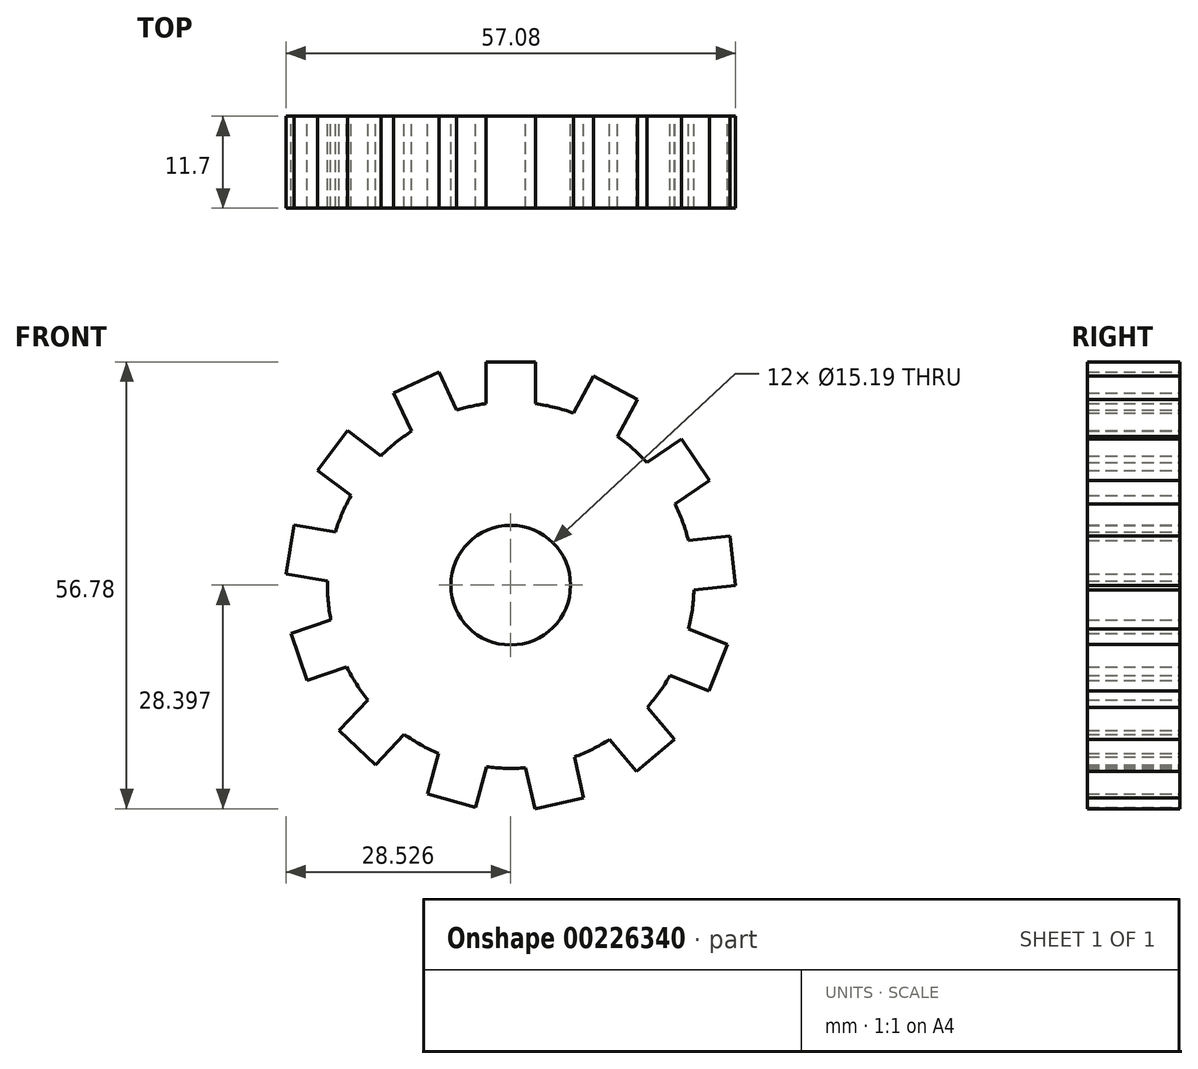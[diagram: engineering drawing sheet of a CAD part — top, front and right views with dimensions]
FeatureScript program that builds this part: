
annotation { "Feature Type Name" : "Feature", "Feature Type Description" : "" }
export const myFeature = defineFeature(function(context is Context, id is Id, definition is map)
    precondition{}
    {
        {
            var Q0;
            Q0=qCreatedBy(makeId("Front.planeOp"),FACE);
            var sketch = newSketch(context, id + "F0", { "sketchPlane" : qUnion([Q0])});
            skLineSegment(sketch, "E0", {"start": v(-30.28, 27.74) * mm, "end": v(-89.44, 27.74) * mm});
            skArc(sketch, "E1", {"start": v(-30.28, 27.74) * mm, "mid": v(-22.47, 31.5) * mm, "end": v(-20.52, 39.94) * mm});
            skArc(sketch, "E2", {"start": v(-104.67, 60.71) * mm, "mid": v(-107.6, 39.36) * mm, "end": v(-89.44, 27.74) * mm});
            skArc(sketch, "E3", {"start": v(-20.52, 39.94) * mm, "mid": v(-56.17, 76.33) * mm, "end": v(-104.67, 60.71) * mm});
            skArc(sketch, "E4", {"start": v(88.46, 15.8) * mm, "mid": v(96.27, 19.54) * mm, "end": v(98.21, 27.99) * mm});
            skArc(sketch, "E5", {"start": v(14.07, 48.76) * mm, "mid": v(11.14, 27.4) * mm, "end": v(29.3, 15.8) * mm});
            skLineSegment(sketch, "E6", {"start": v(29.3, 15.8) * mm, "end": v(88.46, 15.8) * mm});
            skPoint(sketch, "E7.orphan", {"position": v(14.1, 15.8) * mm});
            skArc(sketch, "E8.trimOffspring", {"start": v(98.21, 27.99) * mm, "mid": v(62.56, 64.38) * mm, "end": v(14.07, 48.76) * mm});
            skPoint(sketch, "E9.center.orphan", {"position": v(64.1, 15.8) * mm});
            skArc(sketch, "E10", {"start": v(-57.41, -24.88) * mm, "mid": v(-59.44, -26.34) * mm, "end": v(-61.3, -28.02) * mm});
            skLineSegment(sketch, "E11", {"start": v(-44.8, -21.17) * mm, "end": v(-44.8, -4.69) * mm, "construction": true});
            skLineSegment(sketch, "E12.bottom", {"start": v(20.07, -37.79) * mm, "end": v(51.91, -37.79) * mm, "construction": true});
            skLineSegment(sketch, "E12.top", {"start": v(20.07, -56.1) * mm, "end": v(51.91, -56.1) * mm, "construction": true});
            skLineSegment(sketch, "E12.left", {"start": v(20.07, -37.79) * mm, "end": v(20.07, -56.1) * mm, "construction": true});
            skLineSegment(sketch, "E12.right", {"start": v(51.91, -37.79) * mm, "end": v(51.91, -56.1) * mm, "construction": true});
            skCircle(sketch, "E13", {"center": v(85.83, -43.2) * mm, "radius": 12.55 * mm, "construction": true});
            skLineSegment(sketch, "E14", {"start": v(-47.96, -21.38) * mm, "end": v(-47.96, -16.06) * mm});
            skLineSegment(sketch, "E15", {"start": v(-47.96, -16.06) * mm, "end": v(-41.64, -16.06) * mm});
            skLineSegment(sketch, "E16", {"start": v(-41.64, -16.06) * mm, "end": v(-41.64, -21.38) * mm});
            skPoint(sketch, "E17", {"position": v(-44.8, -16.06) * mm});
            skLineSegment(sketch, "E18.1.0", {"start": v(-36.8, -22.59) * mm, "end": v(-34.3, -17.88) * mm});
            skLineSegment(sketch, "E18.1.1", {"start": v(-34.3, -17.88) * mm, "end": v(-28.72, -20.84) * mm});
            skLineSegment(sketch, "E18.1.2", {"start": v(-28.72, -20.84) * mm, "end": v(-31.22, -25.55) * mm});
            skLineSegment(sketch, "E18.2.0", {"start": v(-27.5, -28.88) * mm, "end": v(-23.1, -25.89) * mm});
            skLineSegment(sketch, "E18.2.1", {"start": v(-23.1, -25.89) * mm, "end": v(-19.55, -31.12) * mm});
            skLineSegment(sketch, "E18.2.2", {"start": v(-19.55, -31.12) * mm, "end": v(-23.95, -34.1) * mm});
            skLineSegment(sketch, "E18.3.0", {"start": v(-22.23, -38.8) * mm, "end": v(-16.93, -38.21) * mm});
            skLineSegment(sketch, "E18.3.1", {"start": v(-16.93, -38.21) * mm, "end": v(-16.25, -44.5) * mm});
            skLineSegment(sketch, "E18.3.2", {"start": v(-16.25, -44.5) * mm, "end": v(-21.54, -45.07) * mm});
            skLineSegment(sketch, "E18.4.0", {"start": v(-22.2, -50.02) * mm, "end": v(-17.26, -51.98) * mm});
            skLineSegment(sketch, "E18.4.1", {"start": v(-17.26, -51.98) * mm, "end": v(-19.6, -57.86) * mm});
            skLineSegment(sketch, "E18.4.2", {"start": v(-19.6, -57.86) * mm, "end": v(-24.54, -55.9) * mm});
            skLineSegment(sketch, "E18.5.0", {"start": v(-27.45, -59.95) * mm, "end": v(-24, -64) * mm});
            skLineSegment(sketch, "E18.5.1", {"start": v(-24, -64) * mm, "end": v(-28.8, -68.1) * mm});
            skLineSegment(sketch, "E18.5.2", {"start": v(-28.8, -68.1) * mm, "end": v(-32.26, -64.05) * mm});
            skLineSegment(sketch, "E18.6.0", {"start": v(-36.73, -66.27) * mm, "end": v(-35.58, -71.47) * mm});
            skLineSegment(sketch, "E18.6.1", {"start": v(-35.58, -71.47) * mm, "end": v(-41.75, -72.84) * mm});
            skLineSegment(sketch, "E18.6.2", {"start": v(-41.75, -72.84) * mm, "end": v(-42.9, -67.64) * mm});
            skLineSegment(sketch, "E18.7.0", {"start": v(-47.89, -67.51) * mm, "end": v(-49.3, -72.64) * mm});
            skLineSegment(sketch, "E18.7.1", {"start": v(-49.3, -72.64) * mm, "end": v(-55.4, -70.96) * mm});
            skLineSegment(sketch, "E18.7.2", {"start": v(-55.4, -70.96) * mm, "end": v(-53.98, -65.83) * mm});
            skLineSegment(sketch, "E18.8.0", {"start": v(-58.33, -63.38) * mm, "end": v(-61.98, -67.26) * mm});
            skLineSegment(sketch, "E18.8.1", {"start": v(-61.98, -67.26) * mm, "end": v(-66.58, -62.92) * mm});
            skLineSegment(sketch, "E18.8.2", {"start": v(-66.58, -62.92) * mm, "end": v(-62.93, -59.05) * mm});
            skLineSegment(sketch, "E18.9.0", {"start": v(-65.62, -54.85) * mm, "end": v(-70.66, -56.56) * mm});
            skLineSegment(sketch, "E18.9.1", {"start": v(-70.66, -56.56) * mm, "end": v(-72.7, -50.57) * mm});
            skLineSegment(sketch, "E18.9.2", {"start": v(-72.7, -50.57) * mm, "end": v(-67.65, -48.86) * mm});
            skLineSegment(sketch, "E18.10.0", {"start": v(-68.07, -43.89) * mm, "end": v(-73.33, -43.04) * mm});
            skLineSegment(sketch, "E18.10.1", {"start": v(-73.33, -43.04) * mm, "end": v(-72.32, -36.8) * mm});
            skLineSegment(sketch, "E18.10.2", {"start": v(-72.32, -36.8) * mm, "end": v(-67.06, -37.65) * mm});
            skLineSegment(sketch, "E18.11.0", {"start": v(-65.1, -33.06) * mm, "end": v(-69.35, -29.85) * mm});
            skLineSegment(sketch, "E18.11.1", {"start": v(-69.35, -29.85) * mm, "end": v(-65.54, -24.8) * mm});
            skLineSegment(sketch, "E18.11.2", {"start": v(-65.54, -24.8) * mm, "end": v(-61.3, -28.02) * mm});
            skLineSegment(sketch, "E18.12.0", {"start": v(-57.41, -24.88) * mm, "end": v(-59.66, -20.06) * mm});
            skLineSegment(sketch, "E18.12.1", {"start": v(-59.66, -20.06) * mm, "end": v(-53.93, -17.38) * mm});
            skLineSegment(sketch, "E18.12.2", {"start": v(-53.93, -17.38) * mm, "end": v(-51.68, -22.2) * mm});
            skLineSegment(sketch, "E18.anchor1", {"start": v(-44.8, -44.44) * mm, "end": v(-47.96, -21.38) * mm, "construction": true});
            skLineSegment(sketch, "E18.anchor2", {"start": v(-44.8, -44.44) * mm, "end": v(-57.41, -24.88) * mm, "construction": true});
            skArc(sketch, "E19.trimOffspring", {"start": v(-47.96, -21.38) * mm, "mid": v(-49.84, -21.72) * mm, "end": v(-51.68, -22.2) * mm});
            skArc(sketch, "E20.trimOffspring", {"start": v(-36.8, -22.59) * mm, "mid": v(-39.19, -21.86) * mm, "end": v(-41.64, -21.38) * mm});
            skArc(sketch, "E21.trimOffspring", {"start": v(-27.5, -28.88) * mm, "mid": v(-29.27, -27.11) * mm, "end": v(-31.22, -25.55) * mm});
            skArc(sketch, "E22.trimOffspring", {"start": v(-22.23, -38.8) * mm, "mid": v(-22.96, -36.4) * mm, "end": v(-23.95, -34.1) * mm});
            skArc(sketch, "E23.trimOffspring", {"start": v(-22.2, -50.02) * mm, "mid": v(-21.74, -47.56) * mm, "end": v(-21.54, -45.07) * mm});
            skArc(sketch, "E24.trimOffspring", {"start": v(-27.45, -59.95) * mm, "mid": v(-25.89, -58) * mm, "end": v(-24.54, -55.9) * mm});
            skArc(sketch, "E25.trimOffspring", {"start": v(-36.73, -66.27) * mm, "mid": v(-34.43, -65.28) * mm, "end": v(-32.26, -64.05) * mm});
            skArc(sketch, "E26.trimOffspring", {"start": v(-47.89, -67.51) * mm, "mid": v(-45.4, -67.7) * mm, "end": v(-42.9, -67.64) * mm});
            skArc(sketch, "E27.trimOffspring", {"start": v(-58.33, -63.38) * mm, "mid": v(-56.22, -64.72) * mm, "end": v(-53.98, -65.83) * mm});
            skArc(sketch, "E28.trimOffspring", {"start": v(-65.62, -54.85) * mm, "mid": v(-64.39, -57.02) * mm, "end": v(-62.93, -59.05) * mm});
            skArc(sketch, "E29.trimOffspring", {"start": v(-68.07, -43.89) * mm, "mid": v(-68, -46.39) * mm, "end": v(-67.65, -48.86) * mm});
            skArc(sketch, "E30.trimOffspring", {"start": v(-65.1, -33.06) * mm, "mid": v(-66.2, -35.3) * mm, "end": v(-67.06, -37.65) * mm});
            skCircle(sketch, "E31", {"center": v(-44.8, -44.44) * mm, "radius": 7.6 * mm});
            skSolve(sketch);
        }
        {
            var Q0;
            Q0=makeQuery(id+"F0.imprint","IMPRINT",FACE,{"disambiguationData":[TD([[makeQuery(id+"F0.imprint","IMPRINT",EDGE,{"derivedFrom":sQuery(id+"F0.wireOp",EDGE,"E10")}),1.0]])]});
            extrude(context, id + "F1", {"entities" : qUnion([Q0]), "depth" : 11.7 * mm});
        }
    });
